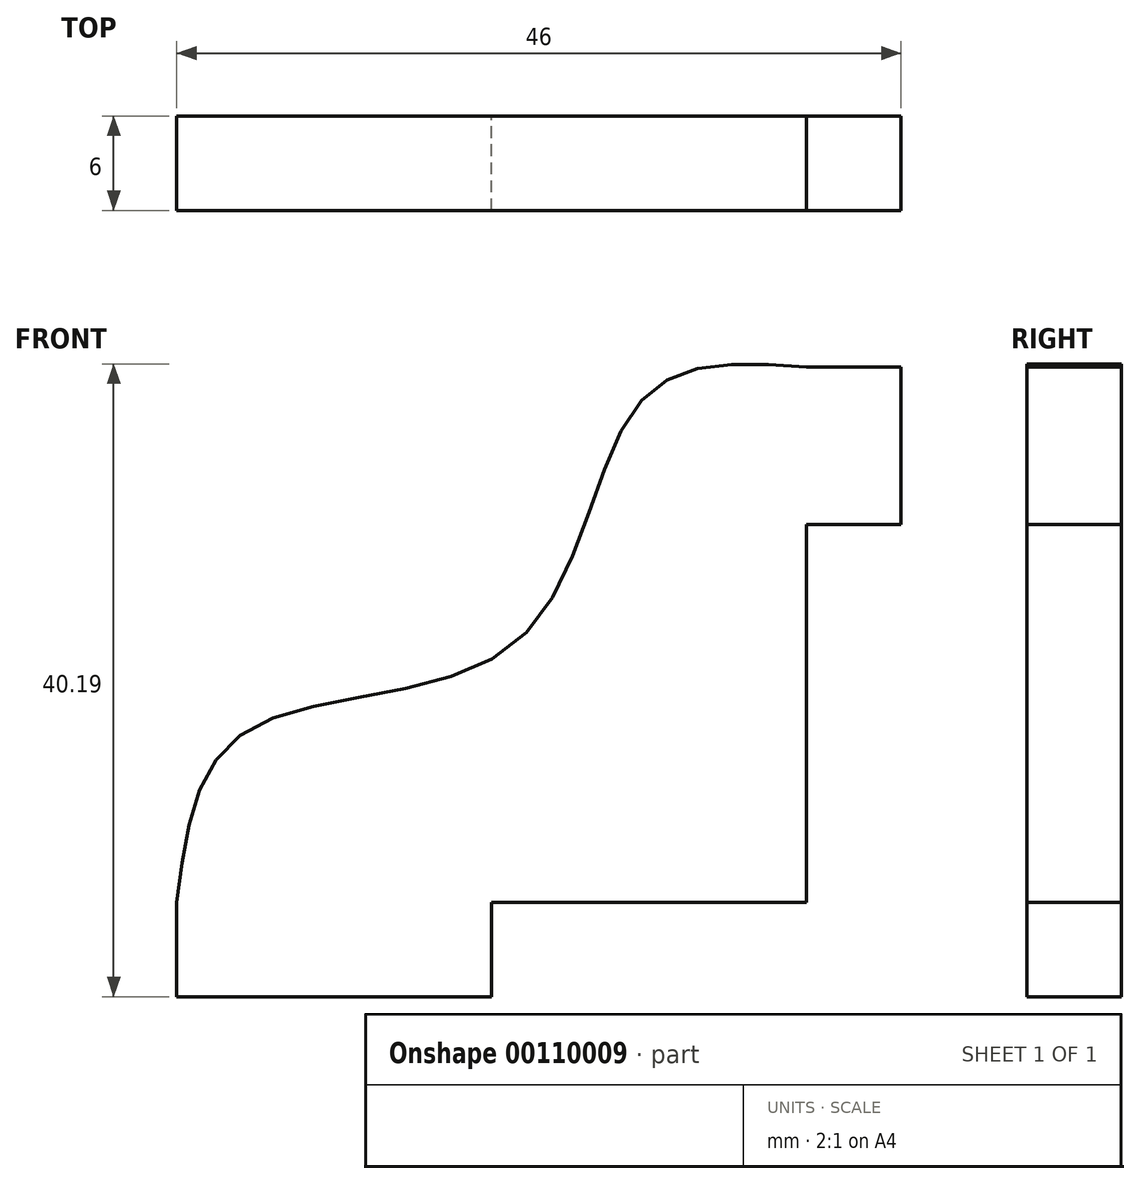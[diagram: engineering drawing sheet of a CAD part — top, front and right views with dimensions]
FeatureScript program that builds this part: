
annotation { "Feature Type Name" : "Feature", "Feature Type Description" : "" }
export const myFeature = defineFeature(function(context is Context, id is Id, definition is map)
    precondition{}
    {
        {
            var Q0;
            Q0=qCreatedBy(makeId("Front.planeOp"),FACE);
            var sketch = newSketch(context, id + "F0", { "sketchPlane" : qUnion([Q0])});
            skLineSegment(sketch, "E0", {"start": v(0, 0) * mm, "end": v(0, 24) * mm});
            skLineSegment(sketch, "E1", {"start": v(0, 24) * mm, "end": v(6, 24) * mm});
            skLineSegment(sketch, "E2", {"start": v(6, 24) * mm, "end": v(6, 34) * mm});
            skLineSegment(sketch, "E3", {"start": v(6, 34) * mm, "end": v(0, 34) * mm});
            skLineSegment(sketch, "E4", {"start": v(0, 0) * mm, "end": v(-20, 0) * mm});
            skLineSegment(sketch, "E5", {"start": v(-20, 0) * mm, "end": v(-20, -6) * mm});
            skLineSegment(sketch, "E6", {"start": v(-20, -6) * mm, "end": v(-40, -6) * mm});
            skLineSegment(sketch, "E7", {"start": v(-40, -6) * mm, "end": v(-40, 0) * mm});
            skFitSpline(sketch, "E8", {"points": [v(0, 34) * mm, v(-10.45, 31.93) * mm, v(-18.41, 16.54) * mm, v(-35.57, 10.88) * mm, v(-40, 0) * mm], "startDerivative": vector(-55.74, 4.14) * mm, "endDerivative": vector(-7.08, -57.86) * mm});
            skSolve(sketch);
        }
        {
            var Q0;
            Q0 = qSketchRegion(id + "F0", true);
            extrude(context, id + "F1", {"entities" : qUnion([Q0]), "depth" : 6 * mm});
        }
    });
